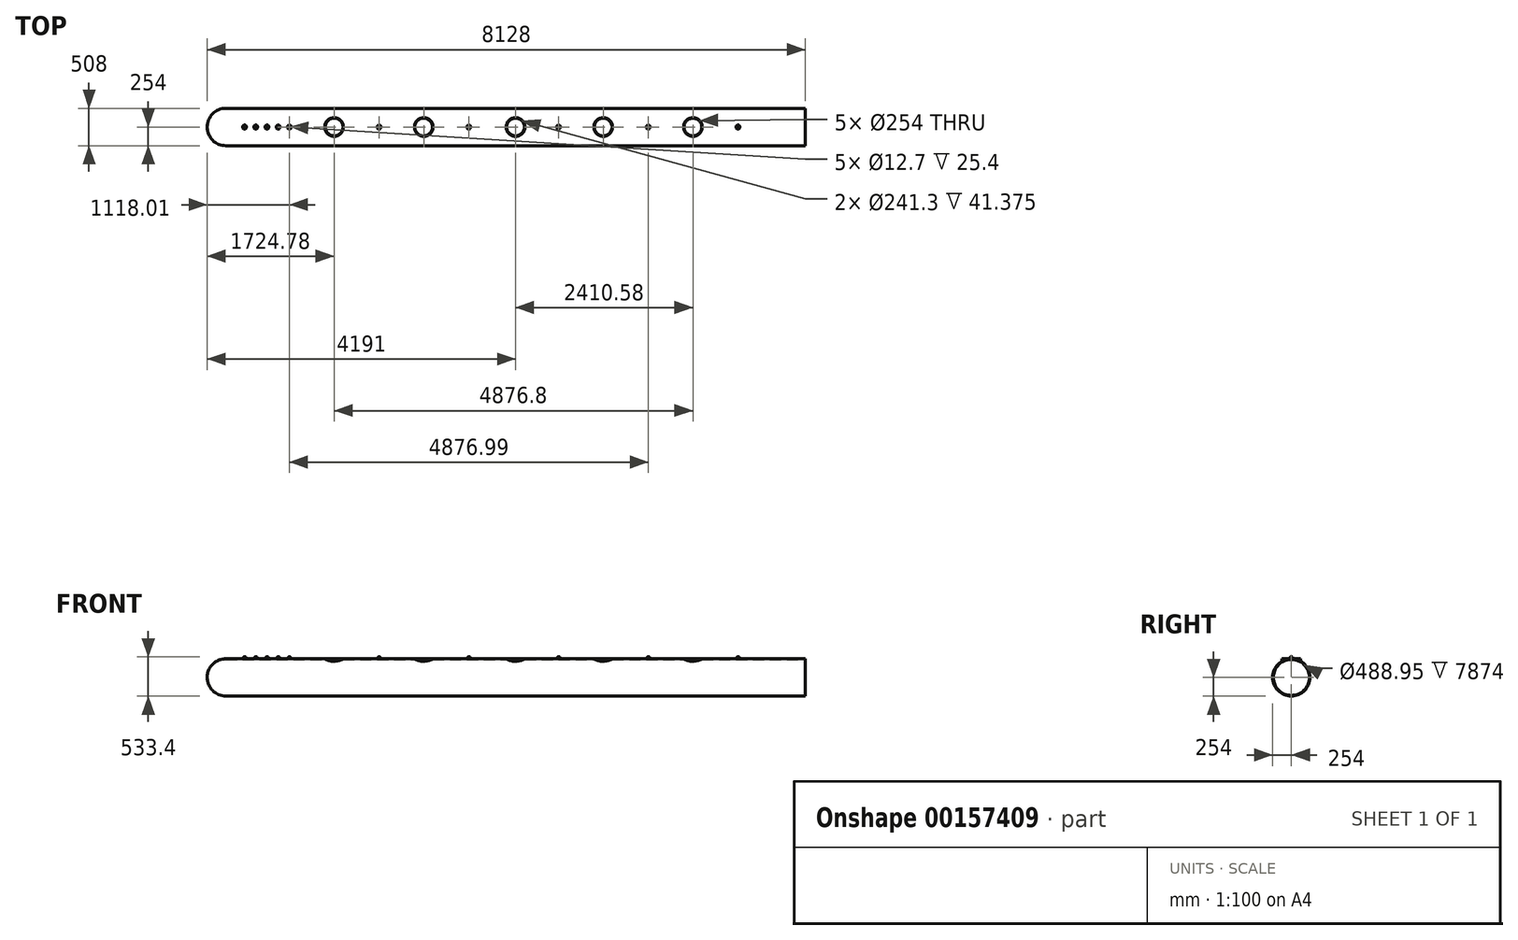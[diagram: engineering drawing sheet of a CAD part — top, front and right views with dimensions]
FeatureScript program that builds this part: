
annotation { "Feature Type Name" : "Feature", "Feature Type Description" : "" }
export const myFeature = defineFeature(function(context is Context, id is Id, definition is map)
    precondition{}
    {
        {
            var Q0;
            Q0=qCreatedBy(makeId("Front.planeOp"),FACE);
            var sketch = newSketch(context, id + "F0", { "sketchPlane" : qUnion([Q0])});
            skLineSegment(sketch, "E0.bottom", {"start": v(3937, 127) * mm, "end": v(-3937, 127) * mm});
            skLineSegment(sketch, "E0.top", {"start": v(3937, -127) * mm, "end": v(-3937, -127) * mm});
            skLineSegment(sketch, "E0.left", {"start": v(3937, 127) * mm, "end": v(3937, -127) * mm});
            skLineSegment(sketch, "E0.right", {"start": v(-3937, 127) * mm, "end": v(-3937, -127) * mm});
            skPoint(sketch, "E0.middle", {"position": v(0, 0) * mm});
            skArc(sketch, "E1", {"start": v(-3937, 127) * mm, "mid": v(-4116.6, 52.6) * mm, "end": v(-4191, -127) * mm});
            skLineSegment(sketch, "E2", {"start": v(-3937, -127) * mm, "end": v(-4191, -127) * mm});
            skSolve(sketch);
        }
        {
            var Q0;
            Q0=qSketchRegion(id+"F0",true);
            var Q1;
            Q1=sQuery(id+"F0.wireOp",EDGE,"E0.top");
            revolve(context, id + "F1", {"entities" : qUnion([Q0]), "axis" : qUnion([Q1]), "revolveType" : RevolveType.FULL});
        }
        {
            var Q0;
            Q0=makeQuery(id+"F1.opRevolve","SWEPT_FACE",FACE,{"disambiguationData":[OSD([sQuery(id+"F0.wireOp",EDGE,"E0.left")])]});
            shell(context, id + "F2", {"entities" : qUnion([Q0]), "thickness" : 9.52 * mm});
        }
        {
            var Q0;
            Q0=qCreatedBy(makeId("Top.planeOp"),FACE);
            var sketch = newSketch(context, id + "F3", { "sketchPlane" : qUnion([Q0])});
            skLineSegment(sketch, "E3", {"start": v(-3939.42, 0) * mm, "end": v(-3685.42, 0) * mm});
            skLineSegment(sketch, "E4", {"start": v(-3685.42, 0) * mm, "end": v(-2466.22, 0) * mm});
            skLineSegment(sketch, "E5", {"start": v(-2466.22, 0) * mm, "end": v(-1247.02, 0) * mm});
            skLineSegment(sketch, "E6", {"start": v(-1247.02, 0) * mm, "end": v(-27.82, 0) * mm});
            skLineSegment(sketch, "E7", {"start": v(-27.82, 0) * mm, "end": v(1191.38, 0) * mm});
            skCircle(sketch, "E8", {"center": v(-2466.22, 0) * mm, "radius": 127 * mm});
            skCircle(sketch, "E9", {"center": v(-1247.02, 0) * mm, "radius": 127 * mm});
            skCircle(sketch, "E10", {"center": v(0, 0) * mm, "radius": 127 * mm});
            skCircle(sketch, "E11", {"center": v(1191.38, 0) * mm, "radius": 127 * mm});
            skLineSegment(sketch, "E12", {"start": v(1191.38, 0) * mm, "end": v(2410.58, 0) * mm});
            skCircle(sketch, "E13", {"center": v(2410.58, 0) * mm, "radius": 127 * mm});
            skCircle(sketch, "E14", {"center": v(-2466.22, 0) * mm, "radius": 120.65 * mm});
            skCircle(sketch, "E15", {"center": v(-1247.02, 0) * mm, "radius": 120.65 * mm});
            skCircle(sketch, "E16", {"center": v(0, 0) * mm, "radius": 120.65 * mm});
            skCircle(sketch, "E17", {"center": v(1191.38, 0) * mm, "radius": 120.65 * mm});
            skCircle(sketch, "E18", {"center": v(2410.58, 0) * mm, "radius": 120.65 * mm});
            skSolve(sketch);
        }
        {
            var Q0;
            Q0 = qSketchRegion(id + "F3", true);
            extrude(context, id + "F4", {"entities" : qUnion([Q0]), "operationType" : NewBodyOperationType.REMOVE, "depth" : 152.4 * mm});
        }
        {
            var Q0;
            Q0=qCreatedBy(makeId("Top.planeOp"),FACE);
            cPlane(context, id + "F5", {"entities" : qUnion([Q0]), "cplaneType" : CPlaneType.OFFSET, "offset" : 101.6 * mm, "width" : 152.4 * mm, "height" : 152.4 * mm});
        }
        {
            var Q0;
            Q0=qCreatedBy(id+"F5.planeOp",FACE);
            var sketch = newSketch(context, id + "F6", { "sketchPlane" : qUnion([Q0])});
            skLineSegment(sketch, "E19", {"start": v(-3682.6, 0) * mm, "end": v(-3073, 0) * mm});
            skLineSegment(sketch, "E20", {"start": v(-3073, 0) * mm, "end": v(-1853.8, 0) * mm});
            skLineSegment(sketch, "E21", {"start": v(-1853.8, 0) * mm, "end": v(-634.6, 0) * mm});
            skLineSegment(sketch, "E22", {"start": v(-634.6, 0) * mm, "end": v(584.6, 0) * mm});
            skLineSegment(sketch, "E23", {"start": v(584.6, 0) * mm, "end": v(1803.8, 0) * mm});
            skCircle(sketch, "E24", {"center": v(-3073, 0) * mm, "radius": 15.88 * mm});
            skCircle(sketch, "E25", {"center": v(-1853.8, 0) * mm, "radius": 15.88 * mm});
            skCircle(sketch, "E26", {"center": v(-634.6, 0) * mm, "radius": 15.88 * mm});
            skCircle(sketch, "E27", {"center": v(584.6, 0) * mm, "radius": 15.88 * mm});
            skCircle(sketch, "E28", {"center": v(1803.8, 0) * mm, "radius": 15.88 * mm});
            skLineSegment(sketch, "E29", {"start": v(-3073, 0) * mm, "end": v(-3225.4, 0) * mm});
            skLineSegment(sketch, "E30", {"start": v(-3225.4, 0) * mm, "end": v(-3377.8, 0) * mm});
            skLineSegment(sketch, "E31", {"start": v(-3377.8, 0) * mm, "end": v(-3530.2, 0) * mm});
            skCircle(sketch, "E32", {"center": v(-3225.4, 0) * mm, "radius": 15.88 * mm});
            skCircle(sketch, "E33", {"center": v(-3377.8, 0) * mm, "radius": 15.88 * mm});
            skCircle(sketch, "E34", {"center": v(-3530.2, 0) * mm, "radius": 15.88 * mm});
            skCircle(sketch, "E35", {"center": v(-3682.6, 0) * mm, "radius": 15.88 * mm});
            skLineSegment(sketch, "E36", {"start": v(1803.8, 0) * mm, "end": v(3023, 0) * mm});
            skCircle(sketch, "E37", {"center": v(3023, 0) * mm, "radius": 15.88 * mm});
            skSolve(sketch);
        }
        {
            var Q0;
            Q0 = qSketchRegion(id + "F6", true);
            extrude(context, id + "F7", {"entities" : qUnion([Q0]), "operationType" : NewBodyOperationType.ADD, "depth" : 50.8 * mm});
        }
        {
            var Q0;
            Q0=makeQuery(id+"F7.opExtrude","CAP_FACE",FACE,{"disambiguationData":[OSD([sQuery(id+"F6.wireOp",EDGE,"E24")])],"isStart":false});
            var sketch = newSketch(context, id + "F8", { "sketchPlane" : qUnion([Q0])});
            skCircle(sketch, "E38", {"center": v(-3073, 0) * mm, "radius": 6.35 * mm});
            skCircle(sketch, "E39", {"center": v(-1854, 0) * mm, "radius": 6.35 * mm});
            skCircle(sketch, "E40", {"center": v(-634.7, 0) * mm, "radius": 6.35 * mm});
            skCircle(sketch, "E41", {"center": v(584.59, 0) * mm, "radius": 6.35 * mm});
            skCircle(sketch, "E42", {"center": v(1804, 0) * mm, "radius": 6.35 * mm});
            skSolve(sketch);
        }
        {
            var Q0;
            Q0 = qSketchRegion(id + "F8", true);
            extrude(context, id + "F9", {"entities" : qUnion([Q0]), "operationType" : NewBodyOperationType.REMOVE, "oppositeDirection" : true, "depth" : 63.5 * mm});
        }
        {
            var Q0;
            Q0=makeQuery(id+"F7.boolean.opBoolean","INTERSECT",EDGE,{"derivedFrom":[makeQuery(id+"F1.opRevolve","SWEPT_FACE",FACE,{"disambiguationData":[OSD([sQuery(id+"F0.wireOp",EDGE,"E0.bottom")])]}),makeQuery(id+"F7.opExtrude","SWEPT_FACE",FACE,{"disambiguationData":[OSD([sQuery(id+"F6.wireOp",EDGE,"E24")])]})]});
            var Q1;
            Q1=makeQuery(id+"F7.boolean.opBoolean","INTERSECT",EDGE,{"derivedFrom":[makeQuery(id+"F1.opRevolve","SWEPT_FACE",FACE,{"disambiguationData":[OSD([sQuery(id+"F0.wireOp",EDGE,"E0.bottom")])]}),makeQuery(id+"F7.opExtrude","SWEPT_FACE",FACE,{"disambiguationData":[OSD([sQuery(id+"F6.wireOp",EDGE,"E25")])]})]});
            var Q2;
            Q2=makeQuery(id+"F7.boolean.opBoolean","INTERSECT",EDGE,{"derivedFrom":[makeQuery(id+"F1.opRevolve","SWEPT_FACE",FACE,{"disambiguationData":[OSD([sQuery(id+"F0.wireOp",EDGE,"E0.bottom")])]}),makeQuery(id+"F7.opExtrude","SWEPT_FACE",FACE,{"disambiguationData":[OSD([sQuery(id+"F6.wireOp",EDGE,"E26")])]})]});
            var Q3;
            Q3=makeQuery(id+"F7.boolean.opBoolean","INTERSECT",EDGE,{"derivedFrom":[makeQuery(id+"F1.opRevolve","SWEPT_FACE",FACE,{"disambiguationData":[OSD([sQuery(id+"F0.wireOp",EDGE,"E0.bottom")])]}),makeQuery(id+"F7.opExtrude","SWEPT_FACE",FACE,{"disambiguationData":[OSD([sQuery(id+"F6.wireOp",EDGE,"E27")])]})]});
            var Q4;
            Q4=makeQuery(id+"F7.boolean.opBoolean","INTERSECT",EDGE,{"derivedFrom":[makeQuery(id+"F1.opRevolve","SWEPT_FACE",FACE,{"disambiguationData":[OSD([sQuery(id+"F0.wireOp",EDGE,"E0.bottom")])]}),makeQuery(id+"F7.opExtrude","SWEPT_FACE",FACE,{"disambiguationData":[OSD([sQuery(id+"F6.wireOp",EDGE,"E28")])]})]});
            var Q5;
            Q5=makeQuery(id+"F7.boolean.opBoolean","INTERSECT",EDGE,{"derivedFrom":[makeQuery(id+"F1.opRevolve","SWEPT_FACE",FACE,{"disambiguationData":[OSD([sQuery(id+"F0.wireOp",EDGE,"E0.bottom")])]}),makeQuery(id+"F7.opExtrude","SWEPT_FACE",FACE,{"disambiguationData":[OSD([sQuery(id+"F6.wireOp",EDGE,"E32")])]})]});
            var Q6;
            Q6=makeQuery(id+"F7.boolean.opBoolean","INTERSECT",EDGE,{"derivedFrom":[makeQuery(id+"F1.opRevolve","SWEPT_FACE",FACE,{"disambiguationData":[OSD([sQuery(id+"F0.wireOp",EDGE,"E0.bottom")])]}),makeQuery(id+"F7.opExtrude","SWEPT_FACE",FACE,{"disambiguationData":[OSD([sQuery(id+"F6.wireOp",EDGE,"E33")])]})]});
            var Q7;
            Q7=makeQuery(id+"F7.boolean.opBoolean","INTERSECT",EDGE,{"derivedFrom":[makeQuery(id+"F1.opRevolve","SWEPT_FACE",FACE,{"disambiguationData":[OSD([sQuery(id+"F0.wireOp",EDGE,"E0.bottom")])]}),makeQuery(id+"F7.opExtrude","SWEPT_FACE",FACE,{"disambiguationData":[OSD([sQuery(id+"F6.wireOp",EDGE,"E34")])]})]});
            var Q8;
            Q8=makeQuery(id+"F7.boolean.opBoolean","INTERSECT",EDGE,{"derivedFrom":[makeQuery(id+"F1.opRevolve","SWEPT_FACE",FACE,{"disambiguationData":[OSD([sQuery(id+"F0.wireOp",EDGE,"E0.bottom")])]}),makeQuery(id+"F7.opExtrude","SWEPT_FACE",FACE,{"disambiguationData":[OSD([sQuery(id+"F6.wireOp",EDGE,"E35")])]})]});
            var Q9;
            Q9=makeQuery(id+"F7.boolean.opBoolean","INTERSECT",EDGE,{"derivedFrom":[makeQuery(id+"F1.opRevolve","SWEPT_FACE",FACE,{"disambiguationData":[OSD([sQuery(id+"F0.wireOp",EDGE,"E0.bottom")])]}),makeQuery(id+"F7.opExtrude","SWEPT_FACE",FACE,{"disambiguationData":[OSD([sQuery(id+"F6.wireOp",EDGE,"E37")])]})]});
            fillet(context, id + "F10", {"entities" : qUnion([Q0, Q1, Q2, Q3, Q4, Q5, Q6, Q7, Q8, Q9]), "radius" : 12.7 * mm, "tangentPropagation" : true, "allowEdgeOverflow" : false});
        }
        {
            var Q0;
            Q0=makeQuery(id+"FoUdTgiShGnCTFw_1.opExtrude","CAP_EDGE",EDGE,{"disambiguationData":[OSD([sQuery(id+"FAXcgHpDmNk0dOG_1.wireOp",EDGE,"GTmVz07m-6xDI-L6cf-gsEY-jet5QeSNXzvg")])],"isStart":false});
            var Q1;
            Q1=makeQuery(id+"F7.opExtrude","CAP_EDGE",EDGE,{"disambiguationData":[OSD([sQuery(id+"F6.wireOp",EDGE,"E28")])],"isStart":false});
            var Q2;
            Q2=makeQuery(id+"F7.opExtrude","CAP_EDGE",EDGE,{"disambiguationData":[OSD([sQuery(id+"F6.wireOp",EDGE,"E27")])],"isStart":false});
            var Q3;
            Q3=makeQuery(id+"F7.opExtrude","CAP_EDGE",EDGE,{"disambiguationData":[OSD([sQuery(id+"F6.wireOp",EDGE,"E26")])],"isStart":false});
            var Q4;
            Q4=makeQuery(id+"F7.opExtrude","CAP_EDGE",EDGE,{"disambiguationData":[OSD([sQuery(id+"F6.wireOp",EDGE,"E25")])],"isStart":false});
            var Q5;
            Q5=makeQuery(id+"F7.opExtrude","CAP_EDGE",EDGE,{"disambiguationData":[OSD([sQuery(id+"F6.wireOp",EDGE,"E24")])],"isStart":false});
            var Q6;
            Q6=makeQuery(id+"F7.opExtrude","CAP_EDGE",EDGE,{"disambiguationData":[OSD([sQuery(id+"F6.wireOp",EDGE,"E33")])],"isStart":false});
            var Q7;
            Q7=makeQuery(id+"F7.opExtrude","CAP_EDGE",EDGE,{"disambiguationData":[OSD([sQuery(id+"F6.wireOp",EDGE,"E34")])],"isStart":false});
            var Q8;
            Q8=makeQuery(id+"F7.opExtrude","CAP_EDGE",EDGE,{"disambiguationData":[OSD([sQuery(id+"F6.wireOp",EDGE,"E35")])],"isStart":false});
            var Q9;
            Q9=makeQuery(id+"F7.opExtrude","CAP_EDGE",EDGE,{"disambiguationData":[OSD([sQuery(id+"F6.wireOp",EDGE,"E32")])],"isStart":false});
            var Q10;
            Q10=makeQuery(id+"F7.opExtrude","CAP_EDGE",EDGE,{"disambiguationData":[OSD([sQuery(id+"F6.wireOp",EDGE,"E37")])],"isStart":false});
            chamfer(context, id + "F11", {"entities" : qUnion([Q0, Q1, Q2, Q3, Q4, Q5, Q6, Q7, Q8, Q9, Q10]), "width" : 1.9 * mm, "tangentPropagation" : true});
        }
        {
            var Q0;
            Q0 = qSketchRegion(id + "F6", true);
            extrude(context, id + "F12", {"entities" : qUnion([Q0]), "operationType" : NewBodyOperationType.ADD, "depth" : 25.4 * mm});
        }
        {
            var Q0;
            Q0 = qSketchRegion(id + "F6", true);
            extrude(context, id + "F13", {"entities" : qUnion([Q0]), "operationType" : NewBodyOperationType.ADD, "depth" : 25.4 * mm});
        }
        {
            var Q0;
            Q0 = qSketchRegion(id + "F3", true);
            extrude(context, id + "F14", {"entities" : qUnion([Q0]), "depth" : 127 * mm});
        }
        {
            var Q0;
            Q0=makeQuery(id+"F1.opRevolve","SWEPT_FACE",FACE,{"disambiguationData":[OSD([sQuery(id+"F0.wireOp",EDGE,"E0.left")])]});
            var sketch = newSketch(context, id + "F15", { "sketchPlane" : qUnion([Q0])});
            skCircle(sketch, "E43", {"center": v(0, -127) * mm, "radius": 244.48 * mm});
            skSolve(sketch);
        }
        {
            var Q0;
            Q0 = qSketchRegion(id + "F15", true);
            extrude(context, id + "F16", {"entities" : qUnion([Q0]), "operationType" : NewBodyOperationType.REMOVE, "oppositeDirection" : true, "depth" : 7874 * mm});
        }
        {
            var Q0;
            Q0=makeQuery(id+"F14.opExtrude","CAP_FACE",FACE,{"disambiguationData":[OSD([sQuery(id+"F3.wireOp",EDGE,"E13"),sQuery(id+"F3.wireOp",EDGE,"E18")])],"isStart":false});
            var sketch = newSketch(context, id + "F17", { "sketchPlane" : qUnion([Q0])});
            skCircle(sketch, "E44", {"center": v(2410.58, 0) * mm, "radius": 120.65 * mm});
            skCircle(sketch, "E45", {"center": v(1191.34, 0) * mm, "radius": 120.65 * mm});
            skCircle(sketch, "E46", {"center": v(0, 0) * mm, "radius": 120.65 * mm});
            skCircle(sketch, "E47", {"center": v(-1248.77, 0) * mm, "radius": 120.65 * mm});
            skCircle(sketch, "E48", {"center": v(-2466.05, 0) * mm, "radius": 120.65 * mm});
            skSolve(sketch);
        }
        {
            var Q0;
            Q0 = qSketchRegion(id + "F17", true);
            extrude(context, id + "F18", {"entities" : qUnion([Q0]), "operationType" : NewBodyOperationType.REMOVE, "oppositeDirection" : true, "depth" : 152.4 * mm});
        }
    });
